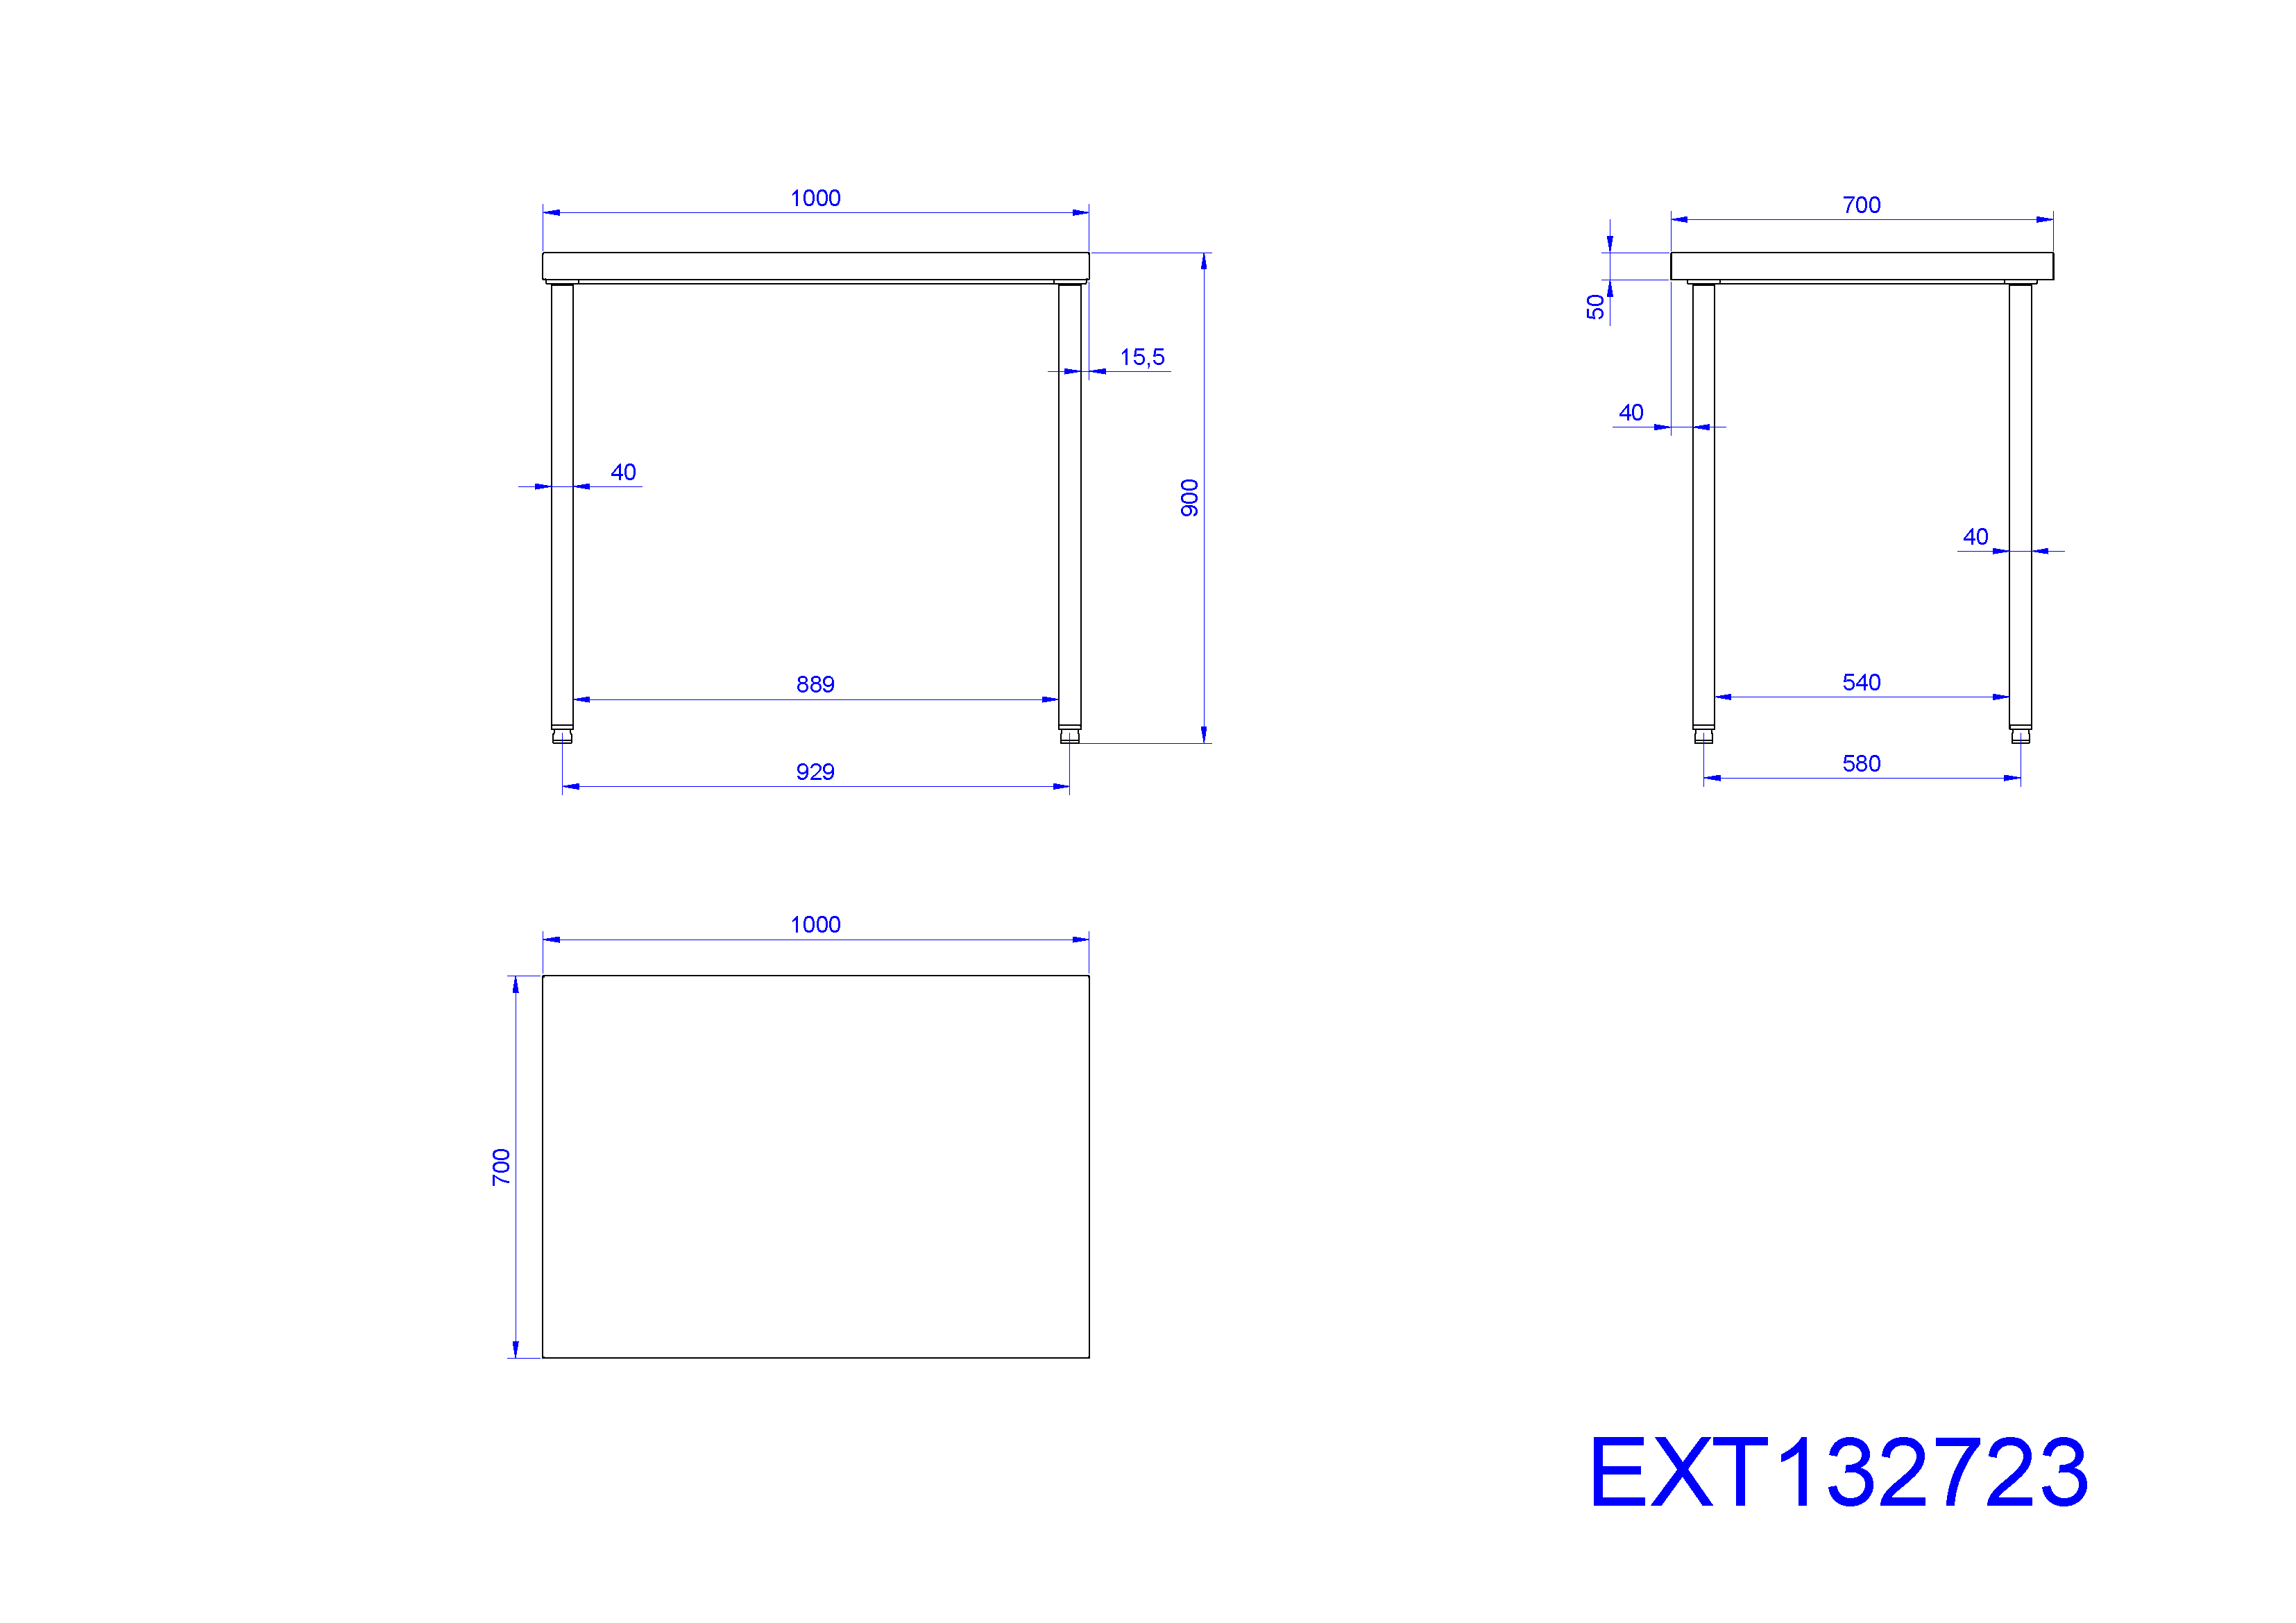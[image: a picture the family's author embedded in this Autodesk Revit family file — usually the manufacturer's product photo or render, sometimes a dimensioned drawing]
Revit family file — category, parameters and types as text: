
# Revit family: QF_ZANUSSI_132915_ML1B0717N
name_source: partatom
category: Attrezzature speciali
units: mm (PartAtom-declared; Revit-internal decimal feet)

## family parameters
Basato su piano di lavoro = No
Condiviso = No
Punto di calcolo locali = No
Quota connettore circolare = Usa diametro
Sempre verticale = Sì
Taglio con vuoti quando caricato = No
Tipo di parte = Normale

## types (1)
- Standard
    Accessory = Sì
    Cold Water Size = 0 mm
    Compressed Air Pressure = 0.0 Pa
    Compressed Air Size = 0 mm
    Compressed Air Volume = 0.0 L/s
    Condensate Return Size = 0 mm
    Cycle = 0 Hz
    Depth Actual = 700 mm  [stored 2.29659 ft]
    Descrizione = CUPBOARD SINK 1 BOWL (500X500) 700MM
    Direct Waste Size = 140 mm
    Gas Input Pressure = 0
    Gas KW = 0
    Gas Size = 0 mm
    HP = 0 HP
    Height Actual = 1000 mm  [stored 3.28084 ft]
    Hot Water Size = 0 mm
    Item Number = 132915
    Length Actual = 700 mm  [stored 2.29659 ft]
    Modello = ML1B0717N
    Phase = 0
    Produttore = Zanussi
    Prospetto di default = 0 mm  [stored 0 ft]
    Refrigerant Compressor Remote = Sì
    Refrigeration Liquid Line Size = 0 mm  [stored 0 ft]
    Refrigeration Suction Line Size = 0 mm  [stored 0 ft]
    Steam Consumption per Hour = 0
    Steam Supply Maximum Pressure = 0.0 Pa
    Steam Supply Minimum Pressure = 0.0 Pa
    Steam Supply Size = 0 mm
    URL = http://www.zanussiprofessional.com
    URL Manufacturer = http://www.zanussiprofessional.com
    Volts = 0 V
    Watts = 0 W
    Weight = 40.00 kg

note: source unit labels omitted for Gas Input Pressure — the stored unit's dimension contradicts the parameter name (converter mislabeling)

note: [stored X ft] marks values corroborated as IEEE doubles in the binary element streams (Revit-internal decimal feet)

## geometry (parser evidence)
native form markers: Sweep x4
no freeform markers — native parametric forms only
